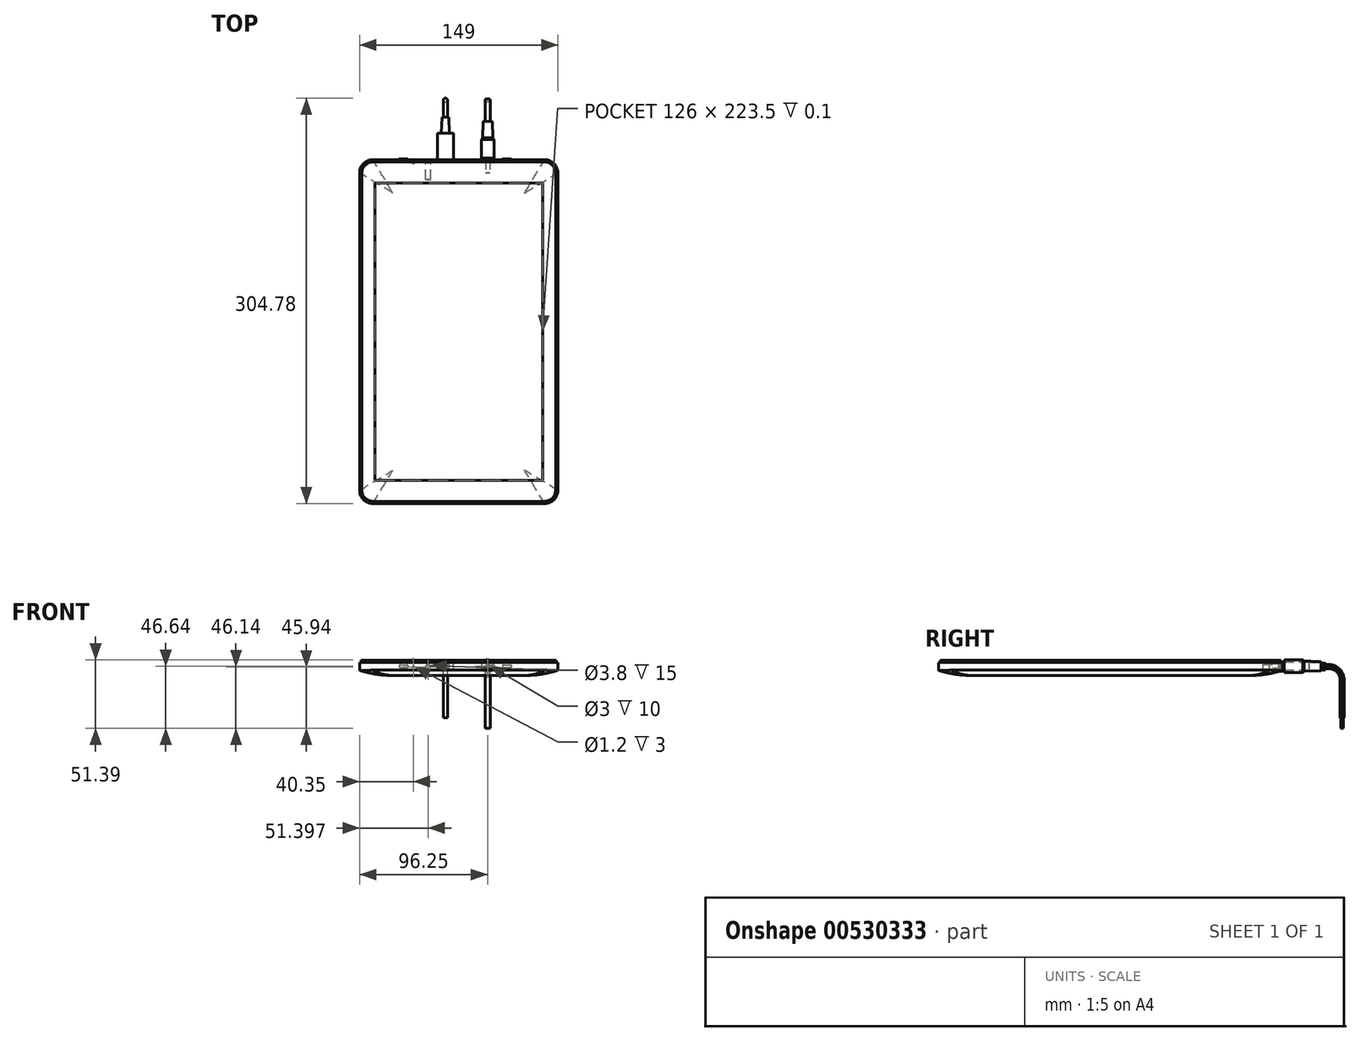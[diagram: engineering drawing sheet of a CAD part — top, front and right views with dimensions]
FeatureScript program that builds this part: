
annotation { "Feature Type Name" : "Feature", "Feature Type Description" : "" }
export const myFeature = defineFeature(function(context is Context, id is Id, definition is map)
    precondition{}
    {
        {
            var Q0;
            Q0=qCreatedBy(makeId("Top.planeOp"),FACE);
            var sketch = newSketch(context, id + "F0", { "sketchPlane" : qUnion([Q0])});
            skLineSegment(sketch, "E0.bottom", {"start": v(74.5, 129.25) * mm, "end": v(-74.5, 129.25) * mm});
            skLineSegment(sketch, "E0.top", {"start": v(74.5, -129.25) * mm, "end": v(-74.5, -129.25) * mm});
            skLineSegment(sketch, "E0.left", {"start": v(74.5, 129.25) * mm, "end": v(74.5, -129.25) * mm});
            skLineSegment(sketch, "E0.right", {"start": v(-74.5, 129.25) * mm, "end": v(-74.5, -129.25) * mm});
            skPoint(sketch, "E0.middle", {"position": v(0, 0) * mm});
            skSolve(sketch);
        }
        {
            var Q0;
            Q0=qCreatedBy(makeId("Front.planeOp"),FACE);
            var sketch = newSketch(context, id + "F1", { "sketchPlane" : qUnion([Q0])});
            skLineSegment(sketch, "E1.bottom", {"start": v(-74.5, 0) * mm, "end": v(74.5, 0) * mm});
            skLineSegment(sketch, "E1.top", {"start": v(-49.5, -11.5) * mm, "end": v(49.5, -11.5) * mm});
            skLineSegment(sketch, "E1.left", {"start": v(-74.5, 0) * mm, "end": v(-74.5, -7.5) * mm});
            skLineSegment(sketch, "E1.right", {"start": v(74.5, 0) * mm, "end": v(74.5, -7.5) * mm});
            skArc(sketch, "E2", {"start": v(-74.5, -7.5) * mm, "mid": v(-62.16, -10.5) * mm, "end": v(-49.5, -11.5) * mm});
            skLineSegment(sketch, "E3", {"start": v(0, 0) * mm, "end": v(0, -11.5) * mm, "construction": true});
            skArc(sketch, "E4.MirrorCS", {"start": v(74.5, -7.5) * mm, "mid": v(62.16, -10.5) * mm, "end": v(49.5, -11.5) * mm});
            skPoint(sketch, "E5.orphan", {"position": v(-74.5, -11.5) * mm});
            skPoint(sketch, "E6.orphan", {"position": v(74.5, -11.5) * mm});
            skSolve(sketch);
        }
        {
            var Q0;
            Q0 = qSketchRegion(id + "F1", true);
            var Q1;
            Q1=sQuery(id+"F0.wireOp",VERTEX,"E0.top.end");
            var Q2;
            Q2=sQuery(id+"F0.wireOp",VERTEX,"E0.bottom.end");
            extrude(context, id + "F2", {"entities" : qUnion([Q0]), "endBound" : BoundingType.UP_TO_VERTEX, "depth" : 25 * mm, "endBoundEntityVertex" : qUnion([Q1]), "offsetDistance" : 25 * mm, "hasSecondDirection" : true, "secondDirectionBound" : SecondDirectionBoundingType.UP_TO_VERTEX, "secondDirectionOppositeDirection" : true, "secondDirectionDepth" : 25 * mm, "secondDirectionBoundEntityVertex" : qUnion([Q2])});
        }
        {
            var Q0;
            Q0=makeQuery(id+"F2.opExtrude","SWEPT_FACE",FACE,{"disambiguationData":[OSD([sQuery(id+"F1.wireOp",EDGE,"E1.left")])]});
            var sketch = newSketch(context, id + "F3", { "sketchPlane" : qUnion([Q0])});
            skArc(sketch, "E7", {"start": v(-129.25, -7.5) * mm, "mid": v(-116.9, -10.5) * mm, "end": v(-104.25, -11.5) * mm});
            skLineSegment(sketch, "E8", {"start": v(0, 0) * mm, "end": v(0, -11.5) * mm, "construction": true});
            skLineSegment(sketch, "E9", {"start": v(-129.25, -7.5) * mm, "end": v(-129.25, -11.5) * mm});
            skLineSegment(sketch, "E10", {"start": v(-129.25, -11.5) * mm, "end": v(-104.25, -11.5) * mm});
            skLineSegment(sketch, "E11.MirrorCS", {"start": v(129.25, -11.5) * mm, "end": v(104.25, -11.5) * mm});
            skLineSegment(sketch, "E12.MirrorCS", {"start": v(129.25, -7.5) * mm, "end": v(129.25, -11.5) * mm});
            skArc(sketch, "E13.MirrorCS", {"start": v(129.25, -7.5) * mm, "mid": v(116.9, -10.5) * mm, "end": v(104.25, -11.5) * mm});
            skSolve(sketch);
        }
        {
            var Q0;
            Q0 = qSketchRegion(id + "F3", true);
            extrude(context, id + "F4", {"entities" : qUnion([Q0]), "operationType" : NewBodyOperationType.REMOVE, "endBound" : BoundingType.THROUGH_ALL, "oppositeDirection" : true, "depth" : 25 * mm, "offsetDistance" : 25 * mm});
        }
        {
            var Q0;
            Q0=makeQuery(id+"F2.opExtrude","CAP_EDGE",EDGE,{"disambiguationData":[OSD([sQuery(id+"F1.wireOp",EDGE,"E1.left")])],"isStart":false});
            var Q1;
            Q1=makeQuery(id+"F2.opExtrude","CAP_EDGE",EDGE,{"disambiguationData":[OSD([sQuery(id+"F1.wireOp",EDGE,"E1.right")])],"isStart":false});
            var Q2;
            Q2=makeQuery(id+"F2.opExtrude","CAP_EDGE",EDGE,{"disambiguationData":[OSD([sQuery(id+"F1.wireOp",EDGE,"E1.right")])],"isStart":true});
            var Q3;
            Q3=makeQuery(id+"F2.opExtrude","CAP_EDGE",EDGE,{"disambiguationData":[OSD([sQuery(id+"F1.wireOp",EDGE,"E1.left")])],"isStart":true});
            fillet(context, id + "F5", {"entities" : qUnion([Q0, Q1, Q2, Q3]), "radius" : 10 * mm, "tangentPropagation" : true, "allowEdgeOverflow" : false});
        }
        {
            var Q0;
            Q0=makeQuery(id+"F2.opExtrude","SWEPT_FACE",FACE,{"disambiguationData":[OSD([sQuery(id+"F1.wireOp",EDGE,"E1.bottom")])]});
            var sketch = newSketch(context, id + "F6", { "sketchPlane" : qUnion([Q0])});
            skArc(sketch, "E14.0", {"start": v(64.5, -129.25) * mm, "mid": v(71.57, -126.32) * mm, "end": v(74.5, -119.25) * mm});
            skLineSegment(sketch, "E14.1", {"start": v(-64.5, -129.25) * mm, "end": v(64.5, -129.25) * mm});
            skLineSegment(sketch, "E14.2", {"start": v(74.5, -119.25) * mm, "end": v(74.5, 119.25) * mm});
            skArc(sketch, "E14.3", {"start": v(-74.5, -119.25) * mm, "mid": v(-71.57, -126.32) * mm, "end": v(-64.5, -129.25) * mm});
            skLineSegment(sketch, "E14.4", {"start": v(-74.5, -119.25) * mm, "end": v(-74.5, 119.25) * mm});
            skArc(sketch, "E14.5", {"start": v(74.5, 119.25) * mm, "mid": v(71.57, 126.32) * mm, "end": v(64.5, 129.25) * mm});
            skLineSegment(sketch, "E14.6", {"start": v(-64.5, 129.25) * mm, "end": v(64.5, 129.25) * mm});
            skArc(sketch, "E14.7", {"start": v(-64.5, 129.25) * mm, "mid": v(-71.57, 126.32) * mm, "end": v(-74.5, 119.25) * mm});
            skArc(sketch, "E15.0", {"start": v(-64.5, 128.05) * mm, "mid": v(-70.72, 125.47) * mm, "end": v(-73.3, 119.25) * mm});
            skLineSegment(sketch, "E15.1", {"start": v(-73.3, -119.25) * mm, "end": v(-73.3, 119.25) * mm});
            skLineSegment(sketch, "E15.2", {"start": v(-64.5, 128.05) * mm, "end": v(64.5, 128.05) * mm});
            skArc(sketch, "E15.3", {"start": v(-73.3, -119.25) * mm, "mid": v(-70.72, -125.47) * mm, "end": v(-64.5, -128.05) * mm});
            skArc(sketch, "E15.4", {"start": v(73.3, 119.25) * mm, "mid": v(70.72, 125.47) * mm, "end": v(64.5, 128.05) * mm});
            skLineSegment(sketch, "E15.5", {"start": v(73.3, -119.25) * mm, "end": v(73.3, 119.25) * mm});
            skArc(sketch, "E15.6", {"start": v(64.5, -128.05) * mm, "mid": v(70.72, -125.47) * mm, "end": v(73.3, -119.25) * mm});
            skLineSegment(sketch, "E15.7", {"start": v(-64.5, -128.05) * mm, "end": v(64.5, -128.05) * mm});
            skLineSegment(sketch, "E16.0", {"start": v(-64.5, -127.55) * mm, "end": v(64.5, -127.55) * mm});
            skArc(sketch, "E16.1", {"start": v(-72.8, -119.25) * mm, "mid": v(-70.37, -125.12) * mm, "end": v(-64.5, -127.55) * mm});
            skArc(sketch, "E16.2", {"start": v(64.5, -127.55) * mm, "mid": v(70.37, -125.12) * mm, "end": v(72.8, -119.25) * mm});
            skLineSegment(sketch, "E16.3", {"start": v(-72.8, -119.25) * mm, "end": v(-72.8, 119.25) * mm});
            skLineSegment(sketch, "E16.4", {"start": v(72.8, -119.25) * mm, "end": v(72.8, 119.25) * mm});
            skArc(sketch, "E16.5", {"start": v(72.8, 119.25) * mm, "mid": v(70.37, 125.12) * mm, "end": v(64.5, 127.55) * mm});
            skLineSegment(sketch, "E16.6", {"start": v(-64.5, 127.55) * mm, "end": v(64.5, 127.55) * mm});
            skArc(sketch, "E16.7", {"start": v(-64.5, 127.55) * mm, "mid": v(-70.37, 125.12) * mm, "end": v(-72.8, 119.25) * mm});
            skSolve(sketch);
        }
        {
            var Q0;
            Q0 = qSketchRegion(id + "F6", true);
            extrude(context, id + "F7", {"entities" : qUnion([Q0]), "operationType" : NewBodyOperationType.REMOVE, "oppositeDirection" : true, "depth" : 1.7 * mm, "offsetDistance" : 25 * mm});
        }
        {
            var Q0;
            Q0=makeQuery(id+"F6.imprint","IMPRINT",FACE,{"disambiguationData":[TD([[makeQuery(id+"F6.imprint","IMPRINT",EDGE,{"derivedFrom":sQuery(id+"F6.wireOp",EDGE,"E16.0")}),1.0]])]});
            extrude(context, id + "F8", {"entities" : qUnion([Q0]), "operationType" : NewBodyOperationType.REMOVE, "oppositeDirection" : true, "depth" : .5 * mm, "offsetDistance" : 25 * mm});
        }
        {
            var Q0;
            Q0=makeQuery(id+"F2.opExtrude","CAP_FACE",FACE,{"disambiguationData":[OSD([sQuery(id+"F1.wireOp",EDGE,"E1.bottom"),sQuery(id+"F1.wireOp",EDGE,"E1.top"),sQuery(id+"F1.wireOp",EDGE,"E1.left"),sQuery(id+"F1.wireOp",EDGE,"E1.right"),sQuery(id+"F1.wireOp",EDGE,"E2"),sQuery(id+"F1.wireOp",EDGE,"E4.MirrorCS")])],"isStart":true});
            var sketch = newSketch(context, id + "F9", { "sketchPlane" : qUnion([Q0])});
            skCircle(sketch, "E17", {"center": v(23.1, -5.2) * mm, "radius": 1.9 * mm});
            skCircle(sketch, "E18", {"center": v(23.1, -5.2) * mm, "radius": 3.1 * mm});
            skSolve(sketch);
        }
        {
            var Q0;
            {var subQ0=sQuery(id+"F9.wireOp",EDGE,"E18");var subQ1=makeQuery(id+"F4.boolean.opBoolean","COPY",EDGE,{"derivedFrom":makeQuery(id+"F4.opExtrude","SWEPT_EDGE",EDGE,{"disambiguationData":[OSD([sQuery(id+"F1.wireOp",EDGE,"E1.left"),sQuery(id+"F1.wireOp",EDGE,"E2"),sQuery(id+"F3.wireOp",EDGE,"E7"),sQuery(id+"F3.wireOp",EDGE,"E9")])]})});var subQ2=makeQuery(id+"F9.imprint","INTERSECT",VERTEX,{"disambiguationData":[OD(0.0)],"derivedFrom":[subQ1,subQ0]});Q0=makeQuery(id+"F9.imprint","IMPRINT",FACE,{"disambiguationData":[TD([[makeQuery(id+"F9.imprint","IMPRINT",EDGE,{"disambiguationData":[TD([[subQ2,1.0]])],"derivedFrom":subQ0}),1.0]])]});}
            extrude(context, id + "F10", {"entities" : qUnion([Q0]), "operationType" : NewBodyOperationType.ADD, "oppositeDirection" : true, "depth" : 25 * mm, "offsetDistance" : 25 * mm});
        }
        {
            var Q0;
            Q0=makeQuery(id+"F9.imprint","IMPRINT",FACE,{"disambiguationData":[TD([[makeQuery(id+"F9.imprint","IMPRINT",EDGE,{"derivedFrom":sQuery(id+"F9.wireOp",EDGE,"E17")}),1.0]])]});
            extrude(context, id + "F11", {"entities" : qUnion([Q0]), "operationType" : NewBodyOperationType.REMOVE, "oppositeDirection" : true, "depth" : 15 * mm, "offsetDistance" : 25 * mm});
        }
        {
            var Q0;
            Q0=makeQuery(id+"F4.boolean.opBoolean","INTERSECT",EDGE,{"derivedFrom":[makeQuery(id+"F2.opExtrude","SWEPT_FACE",FACE,{"disambiguationData":[OSD([sQuery(id+"F1.wireOp",EDGE,"E4.MirrorCS")])]}),makeQuery(id+"F4.opExtrude","SWEPT_FACE",FACE,{"disambiguationData":[OSD([sQuery(id+"F3.wireOp",EDGE,"E7")])]})]});
            var Q1;
            Q1=makeQuery(id+"F4.boolean.opBoolean","INTERSECT",EDGE,{"derivedFrom":[makeQuery(id+"F2.opExtrude","SWEPT_FACE",FACE,{"disambiguationData":[OSD([sQuery(id+"F1.wireOp",EDGE,"E4.MirrorCS")])]}),makeQuery(id+"F4.opExtrude","SWEPT_FACE",FACE,{"disambiguationData":[OSD([sQuery(id+"F3.wireOp",EDGE,"E13.MirrorCS")])]})]});
            var Q2;
            Q2=makeQuery(id+"F4.boolean.opBoolean","INTERSECT",EDGE,{"derivedFrom":[makeQuery(id+"F2.opExtrude","SWEPT_FACE",FACE,{"disambiguationData":[OSD([sQuery(id+"F1.wireOp",EDGE,"E2")])]}),makeQuery(id+"F4.opExtrude","SWEPT_FACE",FACE,{"disambiguationData":[OSD([sQuery(id+"F3.wireOp",EDGE,"E7")])]})]});
            var Q3;
            Q3=makeQuery(id+"F4.boolean.opBoolean","INTERSECT",EDGE,{"derivedFrom":[makeQuery(id+"F2.opExtrude","SWEPT_FACE",FACE,{"disambiguationData":[OSD([sQuery(id+"F1.wireOp",EDGE,"E2")])]}),makeQuery(id+"F4.opExtrude","SWEPT_FACE",FACE,{"disambiguationData":[OSD([sQuery(id+"F3.wireOp",EDGE,"E13.MirrorCS")])]})]});
            fillet(context, id + "F12", {"entities" : qUnion([Q0, Q1, Q2, Q3]), "radius" : 32 * mm, "tangentPropagation" : true, "allowEdgeOverflow" : false});
        }
        {
            var Q0;
            {var subQ0=sQuery(id+"F1.wireOp",EDGE,"E2");var subQ1=sQuery(id+"F1.wireOp",EDGE,"E1.left");Q0=makeQuery(id+"F10.boolean.opBoolean","MERGE",FACE,{"derivedFrom":[makeQuery(id+"F2.opExtrude","CAP_FACE",FACE,{"disambiguationData":[OSD([sQuery(id+"F1.wireOp",EDGE,"E1.bottom"),sQuery(id+"F1.wireOp",EDGE,"E1.top"),subQ1,sQuery(id+"F1.wireOp",EDGE,"E1.right"),subQ0,sQuery(id+"F1.wireOp",EDGE,"E4.MirrorCS")])],"isStart":true}),makeQuery(id+"F10.opExtrude","CAP_FACE",FACE,{"disambiguationData":[OSD([subQ1,subQ0,sQuery(id+"F3.wireOp",EDGE,"E7"),sQuery(id+"F3.wireOp",EDGE,"E9"),sQuery(id+"F9.wireOp",EDGE,"E18")])],"isStart":true})]});}
            var sketch = newSketch(context, id + "F13", { "sketchPlane" : qUnion([Q0])});
            skLineSegment(sketch, "E19.bottom", {"start": v(6.5, -3.5) * mm, "end": v(13.5, -3.5) * mm});
            skLineSegment(sketch, "E19.top", {"start": v(6.5, -6) * mm, "end": v(13.5, -6) * mm});
            skLineSegment(sketch, "E19.left", {"start": v(6.5, -3.5) * mm, "end": v(6.5, -6) * mm});
            skLineSegment(sketch, "E19.right", {"start": v(13.5, -3.5) * mm, "end": v(13.5, -6) * mm});
            skSolve(sketch);
        }
        {
            var Q0;
            Q0 = qSketchRegion(id + "F13", true);
            extrude(context, id + "F14", {"entities" : qUnion([Q0]), "operationType" : NewBodyOperationType.REMOVE, "oppositeDirection" : true, "depth" : 5 * mm, "offsetDistance" : 25 * mm});
        }
        {
            var Q0;
            Q0=makeQuery(id+"F14.boolean.opBoolean","COPY",EDGE,{"derivedFrom":makeQuery(id+"F14.opExtrude","SWEPT_EDGE",EDGE,{"disambiguationData":[OSD([sQuery(id+"F13.wireOp",EDGE,"E19.top"),sQuery(id+"F13.wireOp",EDGE,"E19.right")])]})});
            var Q1;
            Q1=makeQuery(id+"F14.boolean.opBoolean","COPY",EDGE,{"derivedFrom":makeQuery(id+"F14.opExtrude","SWEPT_EDGE",EDGE,{"disambiguationData":[OSD([sQuery(id+"F13.wireOp",EDGE,"E19.top"),sQuery(id+"F13.wireOp",EDGE,"E19.left")])]})});
            chamfer(context, id + "F15", {"entities" : qUnion([Q0, Q1]), "width" : 1 * mm, "tangentPropagation" : true});
        }
        {
            var Q0;
            {var subQ0=sQuery(id+"F1.wireOp",EDGE,"E2");var subQ1=sQuery(id+"F1.wireOp",EDGE,"E1.left");Q0=makeQuery(id+"F10.boolean.opBoolean","MERGE",FACE,{"derivedFrom":[makeQuery(id+"F2.opExtrude","CAP_FACE",FACE,{"disambiguationData":[OSD([sQuery(id+"F1.wireOp",EDGE,"E1.bottom"),sQuery(id+"F1.wireOp",EDGE,"E1.top"),subQ1,sQuery(id+"F1.wireOp",EDGE,"E1.right"),subQ0,sQuery(id+"F1.wireOp",EDGE,"E4.MirrorCS")])],"isStart":true}),makeQuery(id+"F10.opExtrude","CAP_FACE",FACE,{"disambiguationData":[OSD([subQ1,subQ0,sQuery(id+"F3.wireOp",EDGE,"E7"),sQuery(id+"F3.wireOp",EDGE,"E9"),sQuery(id+"F9.wireOp",EDGE,"E18")])],"isStart":true})]});}
            var sketch = newSketch(context, id + "F16", { "sketchPlane" : qUnion([Q0])});
            skCircle(sketch, "E20", {"center": v(-21.75, -4.5) * mm, "radius": 1.5 * mm});
            skSolve(sketch);
        }
        {
            var Q0;
            Q0 = qSketchRegion(id + "F16", true);
            extrude(context, id + "F17", {"entities" : qUnion([Q0]), "operationType" : NewBodyOperationType.REMOVE, "oppositeDirection" : true, "depth" : 10 * mm, "offsetDistance" : 25 * mm});
        }
        {
            var Q0;
            Q0=makeQuery(id+"F8.boolean.opBoolean","COPY",FACE,{"derivedFrom":makeQuery(id+"F8.opExtrude","CAP_FACE",FACE,{"disambiguationData":[OSD([sQuery(id+"F6.wireOp",EDGE,"E16.0"),sQuery(id+"F6.wireOp",EDGE,"E16.1"),sQuery(id+"F6.wireOp",EDGE,"E16.2"),sQuery(id+"F6.wireOp",EDGE,"E16.3"),sQuery(id+"F6.wireOp",EDGE,"E16.4"),sQuery(id+"F6.wireOp",EDGE,"E16.5"),sQuery(id+"F6.wireOp",EDGE,"E16.6"),sQuery(id+"F6.wireOp",EDGE,"E16.7")])],"isStart":false})});
            var sketch = newSketch(context, id + "F18", { "sketchPlane" : qUnion([Q0])});
            skLineSegment(sketch, "E21.bottom", {"start": v(-63, 111.75) * mm, "end": v(63, 111.75) * mm});
            skLineSegment(sketch, "E21.top", {"start": v(-63, -111.75) * mm, "end": v(63, -111.75) * mm});
            skLineSegment(sketch, "E21.left", {"start": v(-63, 111.75) * mm, "end": v(-63, -111.75) * mm});
            skLineSegment(sketch, "E21.right", {"start": v(63, 111.75) * mm, "end": v(63, -111.75) * mm});
            skPoint(sketch, "E21.middle", {"position": v(0, 0) * mm});
            skSolve(sketch);
        }
        {
            var Q0;
            Q0 = qSketchRegion(id + "F18", true);
            extrude(context, id + "F19", {"entities" : qUnion([Q0]), "operationType" : NewBodyOperationType.REMOVE, "oppositeDirection" : true, "depth" : .1 * mm, "offsetDistance" : 25 * mm});
        }
        {
            var Q0;
            Q0=makeQuery(id+"F19.boolean.opBoolean","COPY",FACE,{"derivedFrom":makeQuery(id+"F19.opExtrude","CAP_FACE",FACE,{"disambiguationData":[OSD([sQuery(id+"F18.wireOp",EDGE,"E21.bottom"),sQuery(id+"F18.wireOp",EDGE,"E21.top"),sQuery(id+"F18.wireOp",EDGE,"E21.left"),sQuery(id+"F18.wireOp",EDGE,"E21.right")])],"isStart":false})});
            extrude(context, id + "F20", {"entities" : qUnion([Q0]), "depth" : .1 * mm, "offsetDistance" : 25 * mm});
        }
        {
            var Q0;
            Q0=makeQuery(id+"F14.boolean.opBoolean","COPY",FACE,{"derivedFrom":makeQuery(id+"F14.opExtrude","CAP_FACE",FACE,{"disambiguationData":[OSD([sQuery(id+"F13.wireOp",EDGE,"E19.bottom"),sQuery(id+"F13.wireOp",EDGE,"E19.top"),sQuery(id+"F13.wireOp",EDGE,"E19.left"),sQuery(id+"F13.wireOp",EDGE,"E19.right")])],"isStart":false})});
            var Q1;
            {var subQ0=sQuery(id+"F1.wireOp",EDGE,"E2");var subQ1=sQuery(id+"F1.wireOp",EDGE,"E1.left");Q1=makeQuery(id+"F10.boolean.opBoolean","MERGE",FACE,{"derivedFrom":[makeQuery(id+"F2.opExtrude","CAP_FACE",FACE,{"disambiguationData":[OSD([sQuery(id+"F1.wireOp",EDGE,"E1.bottom"),sQuery(id+"F1.wireOp",EDGE,"E1.top"),subQ1,sQuery(id+"F1.wireOp",EDGE,"E1.right"),subQ0,sQuery(id+"F1.wireOp",EDGE,"E4.MirrorCS")])],"isStart":true}),makeQuery(id+"F10.opExtrude","CAP_FACE",FACE,{"disambiguationData":[OSD([subQ1,subQ0,sQuery(id+"F3.wireOp",EDGE,"E7"),sQuery(id+"F3.wireOp",EDGE,"E9"),sQuery(id+"F9.wireOp",EDGE,"E18")])],"isStart":true})]});}
            extrude(context, id + "F21", {"entities" : qUnion([Q0]), "endBound" : BoundingType.UP_TO_SURFACE, "depth" : 5 * mm, "endBoundEntityFace" : qUnion([Q1]), "offsetDistance" : 25 * mm});
        }
        {
            var Q0;
            Q0=makeQuery(id+"F13.imprint","IMPRINT",FACE,{"disambiguationData":[TD([[makeQuery(id+"F13.imprint","IMPRINT",EDGE,{"derivedFrom":sQuery(id+"F13.wireOp",EDGE,"E19.bottom")}),-1.0]])]});
            var sketch = newSketch(context, id + "F22", { "sketchPlane" : qUnion([Q0])});
            skLineSegment(sketch, "E22", {"start": v(10, -3.5) * mm, "end": v(10, -6) * mm, "construction": true});
            skLineSegment(sketch, "E23.bottom", {"start": v(16, -7.75) * mm, "end": v(4, -7.75) * mm});
            skLineSegment(sketch, "E23.top", {"start": v(16, -1.75) * mm, "end": v(4, -1.75) * mm});
            skLineSegment(sketch, "E23.left", {"start": v(16, -7.75) * mm, "end": v(16, -1.75) * mm});
            skLineSegment(sketch, "E23.right", {"start": v(4, -7.75) * mm, "end": v(4, -1.75) * mm});
            skPoint(sketch, "E23.middle", {"position": v(10, -4.75) * mm});
            skSolve(sketch);
        }
        {
            var Q0;
            Q0 = qSketchRegion(id + "F22", true);
            extrude(context, id + "F23", {"entities" : qUnion([Q0]), "operationType" : NewBodyOperationType.ADD, "depth" : 20 * mm, "offsetDistance" : 25 * mm});
        }
        {
            var Q0;
            Q0=makeQuery(id+"F23.opExtrude","CAP_FACE",FACE,{"disambiguationData":[OSD([sQuery(id+"F22.wireOp",EDGE,"E23.bottom"),sQuery(id+"F22.wireOp",EDGE,"E23.top"),sQuery(id+"F22.wireOp",EDGE,"E23.left"),sQuery(id+"F22.wireOp",EDGE,"E23.right")])],"isStart":false});
            var sketch = newSketch(context, id + "F24", { "sketchPlane" : qUnion([Q0])});
            skCircle(sketch, "E24", {"center": v(10, -4.75) * mm, "radius": 3 * mm});
            skSolve(sketch);
        }
        {
            var Q0;
            Q0 = qSketchRegion(id + "F24", true);
            extrude(context, id + "F25", {"entities" : qUnion([Q0]), "operationType" : NewBodyOperationType.ADD, "depth" : 12 * mm, "offsetDistance" : 25 * mm, "hasDraft" : true, "draftAngle" : 2 * degree, "draftPullDirection" : true});
        }
        {
            var Q0;
            Q0=makeQuery(id+"F25.opExtrude","CAP_FACE",FACE,{"disambiguationData":[OSD([sQuery(id+"F24.wireOp",EDGE,"E24")])],"isStart":false});
            var sketch = newSketch(context, id + "F26", { "sketchPlane" : qUnion([Q0])});
            skCircle(sketch, "E25", {"center": v(10, -4.75) * mm, "radius": 1.5 * mm});
            skSolve(sketch);
        }
        {
            var Q0;
            Q0=sQuery(id+"F26.wireOp",VERTEX,"E25.center");
            var Q1;
            Q1=qCreatedBy(makeId("Right.planeOp"),FACE);
            cPlane(context, id + "F27", {"entities" : qUnion([Q0, Q1]), "cplaneType" : CPlaneType.PLANE_POINT, "offset" : 25 * mm, "width" : 150 * mm, "height" : 150 * mm});
        }
        {
            var Q0;
            Q0=qCreatedBy(id+"F27.planeOp",FACE);
            var sketch = newSketch(context, id + "F28", { "sketchPlane" : qUnion([Q0])});
            skLineSegment(sketch, "E26", {"start": v(161.25, -4.75) * mm, "end": v(164.03, -4.75) * mm});
            skLineSegment(sketch, "E27", {"start": v(174.03, -14.75) * mm, "end": v(174.03, -43.12) * mm});
            skPoint(sketch, "E28.visualSharp", {"position": v(174.03, -4.75) * mm});
            skArc(sketch, "E28.filletArc", {"start": v(174.03, -14.75) * mm, "mid": v(171.1, -7.68) * mm, "end": v(164.03, -4.75) * mm});
            skSolve(sketch);
        }
        {
            var Q0;
            Q0 = qSketchRegion(id + "F26", true);
            var Q1;
            Q1=sQuery(id+"F26.wireOp",EDGE,"E25");
            var Q2;
            Q2 = qConstructionFilter(qBodyType(qCreatedBy(id + "F28" ,EDGE), BodyType.WIRE), ConstructionObject.NO);
            sweep(context, id + "F29", {"operationType" : NewBodyOperationType.ADD, "profiles" : qUnion([Q0]), "surfaceProfiles" : qUnion([Q1]), "path" : qUnion([Q2])});
        }
        {
            var Q0;
            Q0=makeQuery(id+"F17.boolean.opBoolean","COPY",FACE,{"derivedFrom":makeQuery(id+"F17.opExtrude","CAP_FACE",FACE,{"disambiguationData":[OSD([sQuery(id+"F16.wireOp",EDGE,"E20")])],"isStart":false})});
            extrude(context, id + "F30", {"entities" : qUnion([Q0]), "depth" : 11.3 * mm, "offsetDistance" : 25 * mm});
        }
        {
            var Q0;
            Q0=makeQuery(id+"F30.opExtrude","CAP_FACE",FACE,{"disambiguationData":[OSD([sQuery(id+"F16.wireOp",EDGE,"E20")])],"isStart":false});
            var sketch = newSketch(context, id + "F31", { "sketchPlane" : qUnion([Q0])});
            skCircle(sketch, "E29", {"center": v(-21.75, -4.5) * mm, "radius": 4.75 * mm});
            skSolve(sketch);
        }
        {
            var Q0;
            Q0 = qSketchRegion(id + "F31", true);
            extrude(context, id + "F32", {"entities" : qUnion([Q0]), "operationType" : NewBodyOperationType.ADD, "depth" : 15 * mm, "offsetDistance" : 25 * mm});
        }
        {
            var Q0;
            Q0=makeQuery(id+"F32.opExtrude","CAP_EDGE",EDGE,{"disambiguationData":[OSD([sQuery(id+"F31.wireOp",EDGE,"E29")])],"isStart":false});
            chamfer(context, id + "F33", {"entities" : qUnion([Q0]), "width" : 1 * mm, "tangentPropagation" : true});
        }
        {
            var Q0;
            Q0=makeQuery(id+"F32.opExtrude","CAP_FACE",FACE,{"disambiguationData":[OSD([sQuery(id+"F31.wireOp",EDGE,"E29")])],"isStart":false});
            extrude(context, id + "F34", {"entities" : qUnion([Q0]), "operationType" : NewBodyOperationType.ADD, "depth" : 12.5 * mm, "offsetDistance" : 25 * mm, "hasDraft" : true, "draftAngle" : 1 * degree, "draftPullDirection" : true});
        }
        {
            var Q0;
            Q0=makeQuery(id+"F34.opExtrude","CAP_FACE",FACE,{"disambiguationData":[OSD([sQuery(id+"F31.wireOp",EDGE,"E29")])],"isStart":false});
            var sketch = newSketch(context, id + "F35", { "sketchPlane" : qUnion([Q0])});
            skCircle(sketch, "E30", {"center": v(-21.75, -4.5) * mm, "radius": 1.82 * mm, "construction": true});
            skLineSegment(sketch, "E31", {"start": v(-20.85, -4.5) * mm, "end": v(-22.65, -4.5) * mm, "construction": true});
            skArc(sketch, "E32.0.startCap", {"start": v(-20.85, -3.58) * mm, "mid": v(-19.93, -4.5) * mm, "end": v(-20.85, -5.43) * mm});
            skArc(sketch, "E32.0.endCap", {"start": v(-22.65, -5.43) * mm, "mid": v(-23.58, -4.5) * mm, "end": v(-22.65, -3.58) * mm});
            skLineSegment(sketch, "E32.0.left", {"start": v(-20.85, -5.42) * mm, "end": v(-22.65, -5.42) * mm});
            skLineSegment(sketch, "E32.0.right", {"start": v(-20.85, -3.58) * mm, "end": v(-22.65, -3.58) * mm});
            skSolve(sketch);
        }
        {
            var Q0;
            Q0=sQuery(id+"F35.wireOp",VERTEX,"E30.center");
            var Q1;
            Q1=qCreatedBy(makeId("Right.planeOp"),FACE);
            cPlane(context, id + "F36", {"entities" : qUnion([Q0, Q1]), "cplaneType" : CPlaneType.PLANE_POINT, "offset" : 25 * mm, "width" : 150 * mm, "height" : 150 * mm});
        }
        {
            var Q0;
            Q0=qCreatedBy(id+"F36.planeOp",FACE);
            var sketch = newSketch(context, id + "F37", { "sketchPlane" : qUnion([Q0])});
            skLineSegment(sketch, "E33", {"start": v(158.05, -4.5) * mm, "end": v(164.03, -4.5) * mm});
            skLineSegment(sketch, "E34", {"start": v(174.03, -14.5) * mm, "end": v(174.03, -51.14) * mm});
            skPoint(sketch, "E35.visualSharp", {"position": v(174.03, -4.5) * mm});
            skArc(sketch, "E35.filletArc", {"start": v(174.03, -14.5) * mm, "mid": v(171.1, -7.43) * mm, "end": v(164.03, -4.5) * mm});
            skSolve(sketch);
        }
        {
            var Q0;
            Q0 = qSketchRegion(id + "F35", true);
            var Q1;
            Q1 = qConstructionFilter(qBodyType(qCreatedBy(id + "F37" ,EDGE), BodyType.WIRE), ConstructionObject.NO);
            sweep(context, id + "F38", {"operationType" : NewBodyOperationType.ADD, "profiles" : qUnion([Q0]), "path" : qUnion([Q1])});
        }
        {
            var Q0;
            {var subQ0=sQuery(id+"F1.wireOp",EDGE,"E2");var subQ1=sQuery(id+"F1.wireOp",EDGE,"E1.left");Q0=makeQuery(id+"F10.boolean.opBoolean","MERGE",FACE,{"derivedFrom":[makeQuery(id+"F2.opExtrude","CAP_FACE",FACE,{"disambiguationData":[OSD([sQuery(id+"F1.wireOp",EDGE,"E1.bottom"),sQuery(id+"F1.wireOp",EDGE,"E1.top"),subQ1,sQuery(id+"F1.wireOp",EDGE,"E1.right"),subQ0,sQuery(id+"F1.wireOp",EDGE,"E4.MirrorCS")])],"isStart":true}),makeQuery(id+"F10.opExtrude","CAP_FACE",FACE,{"disambiguationData":[OSD([subQ1,subQ0,sQuery(id+"F3.wireOp",EDGE,"E7"),sQuery(id+"F3.wireOp",EDGE,"E9"),sQuery(id+"F9.wireOp",EDGE,"E18")])],"isStart":true})]});}
            var sketch = newSketch(context, id + "F39", { "sketchPlane" : qUnion([Q0])});
            skLineSegment(sketch, "E36.bottom", {"start": v(-33.8, -3.5) * mm, "end": v(-38.7, -3.5) * mm});
            skLineSegment(sketch, "E36.top", {"start": v(-33.8, -5.5) * mm, "end": v(-38.7, -5.5) * mm});
            skLineSegment(sketch, "E36.left", {"start": v(-33, -4.3) * mm, "end": v(-33, -4.7) * mm});
            skLineSegment(sketch, "E36.right", {"start": v(-39.5, -4.3) * mm, "end": v(-39.5, -4.7) * mm});
            skPoint(sketch, "E37.visualSharp", {"position": v(-33, -5.5) * mm});
            skArc(sketch, "E37.filletArc", {"start": v(-33.8, -5.5) * mm, "mid": v(-33.23, -5.27) * mm, "end": v(-33, -4.7) * mm});
            skPoint(sketch, "E38.visualSharp", {"position": v(-33, -3.5) * mm});
            skArc(sketch, "E38.filletArc", {"start": v(-33, -4.3) * mm, "mid": v(-33.23, -3.73) * mm, "end": v(-33.8, -3.5) * mm});
            skPoint(sketch, "E39.visualSharp", {"position": v(-39.5, -3.5) * mm});
            skArc(sketch, "E39.filletArc", {"start": v(-38.7, -3.5) * mm, "mid": v(-39.27, -3.73) * mm, "end": v(-39.5, -4.3) * mm});
            skPoint(sketch, "E40.visualSharp", {"position": v(-39.5, -5.5) * mm});
            skArc(sketch, "E40.filletArc", {"start": v(-39.5, -4.7) * mm, "mid": v(-39.27, -5.27) * mm, "end": v(-38.7, -5.5) * mm});
            skSolve(sketch);
        }
        {
            var Q0;
            Q0 = qSketchRegion(id + "F39", true);
            extrude(context, id + "F40", {"entities" : qUnion([Q0]), "operationType" : NewBodyOperationType.ADD, "depth" : .65 * mm, "offsetDistance" : 25 * mm});
        }
        {
            var Q0;
            {var subQ0=sQuery(id+"F1.wireOp",EDGE,"E2");var subQ1=sQuery(id+"F1.wireOp",EDGE,"E1.left");Q0=makeQuery(id+"F10.boolean.opBoolean","MERGE",FACE,{"derivedFrom":[makeQuery(id+"F2.opExtrude","CAP_FACE",FACE,{"disambiguationData":[OSD([sQuery(id+"F1.wireOp",EDGE,"E1.bottom"),sQuery(id+"F1.wireOp",EDGE,"E1.top"),subQ1,sQuery(id+"F1.wireOp",EDGE,"E1.right"),subQ0,sQuery(id+"F1.wireOp",EDGE,"E4.MirrorCS")])],"isStart":true}),makeQuery(id+"F10.opExtrude","CAP_FACE",FACE,{"disambiguationData":[OSD([subQ1,subQ0,sQuery(id+"F3.wireOp",EDGE,"E7"),sQuery(id+"F3.wireOp",EDGE,"E9"),sQuery(id+"F9.wireOp",EDGE,"E18")])],"isStart":true})]});}
            var sketch = newSketch(context, id + "F41", { "sketchPlane" : qUnion([Q0])});
            skLineSegment(sketch, "E41.bottom", {"start": v(43.95, -3.5) * mm, "end": v(39.05, -3.5) * mm});
            skLineSegment(sketch, "E41.top", {"start": v(43.95, -5.5) * mm, "end": v(39.05, -5.5) * mm});
            skLineSegment(sketch, "E41.left", {"start": v(44.75, -4.3) * mm, "end": v(44.75, -4.7) * mm});
            skLineSegment(sketch, "E41.right", {"start": v(38.25, -4.3) * mm, "end": v(38.25, -4.7) * mm});
            skPoint(sketch, "E42.visualSharp", {"position": v(44.75, -5.5) * mm});
            skArc(sketch, "E42.filletArc", {"start": v(43.95, -5.5) * mm, "mid": v(44.52, -5.27) * mm, "end": v(44.75, -4.7) * mm});
            skPoint(sketch, "E43.visualSharp", {"position": v(44.75, -3.5) * mm});
            skArc(sketch, "E43.filletArc", {"start": v(44.75, -4.3) * mm, "mid": v(44.52, -3.73) * mm, "end": v(43.95, -3.5) * mm});
            skPoint(sketch, "E44.visualSharp", {"position": v(38.25, -3.5) * mm});
            skArc(sketch, "E44.filletArc", {"start": v(39.05, -3.5) * mm, "mid": v(38.48, -3.73) * mm, "end": v(38.25, -4.3) * mm});
            skPoint(sketch, "E45.visualSharp", {"position": v(38.25, -5.5) * mm});
            skArc(sketch, "E45.filletArc", {"start": v(38.25, -4.7) * mm, "mid": v(38.48, -5.27) * mm, "end": v(39.05, -5.5) * mm});
            skSolve(sketch);
        }
        {
            var Q0;
            Q0 = qSketchRegion(id + "F41", true);
            extrude(context, id + "F42", {"entities" : qUnion([Q0]), "operationType" : NewBodyOperationType.ADD, "depth" : .65 * mm, "offsetDistance" : 25 * mm});
        }
        {
            var Q0;
            {var subQ0=sQuery(id+"F1.wireOp",EDGE,"E2");var subQ1=sQuery(id+"F1.wireOp",EDGE,"E1.left");Q0=makeQuery(id+"F10.boolean.opBoolean","MERGE",FACE,{"derivedFrom":[makeQuery(id+"F2.opExtrude","CAP_FACE",FACE,{"disambiguationData":[OSD([sQuery(id+"F1.wireOp",EDGE,"E1.bottom"),sQuery(id+"F1.wireOp",EDGE,"E1.top"),subQ1,sQuery(id+"F1.wireOp",EDGE,"E1.right"),subQ0,sQuery(id+"F1.wireOp",EDGE,"E4.MirrorCS")])],"isStart":true}),makeQuery(id+"F10.opExtrude","CAP_FACE",FACE,{"disambiguationData":[OSD([subQ1,subQ0,sQuery(id+"F3.wireOp",EDGE,"E7"),sQuery(id+"F3.wireOp",EDGE,"E9"),sQuery(id+"F9.wireOp",EDGE,"E18")])],"isStart":true})]});}
            var sketch = newSketch(context, id + "F43", { "sketchPlane" : qUnion([Q0])});
            skCircle(sketch, "E46", {"center": v(34.15, -5) * mm, "radius": 0.6 * mm});
            skSolve(sketch);
        }
        {
            var Q0;
            Q0 = qSketchRegion(id + "F43", true);
            extrude(context, id + "F44", {"entities" : qUnion([Q0]), "operationType" : NewBodyOperationType.REMOVE, "oppositeDirection" : true, "depth" : 3 * mm, "offsetDistance" : 25 * mm});
        }
    });
